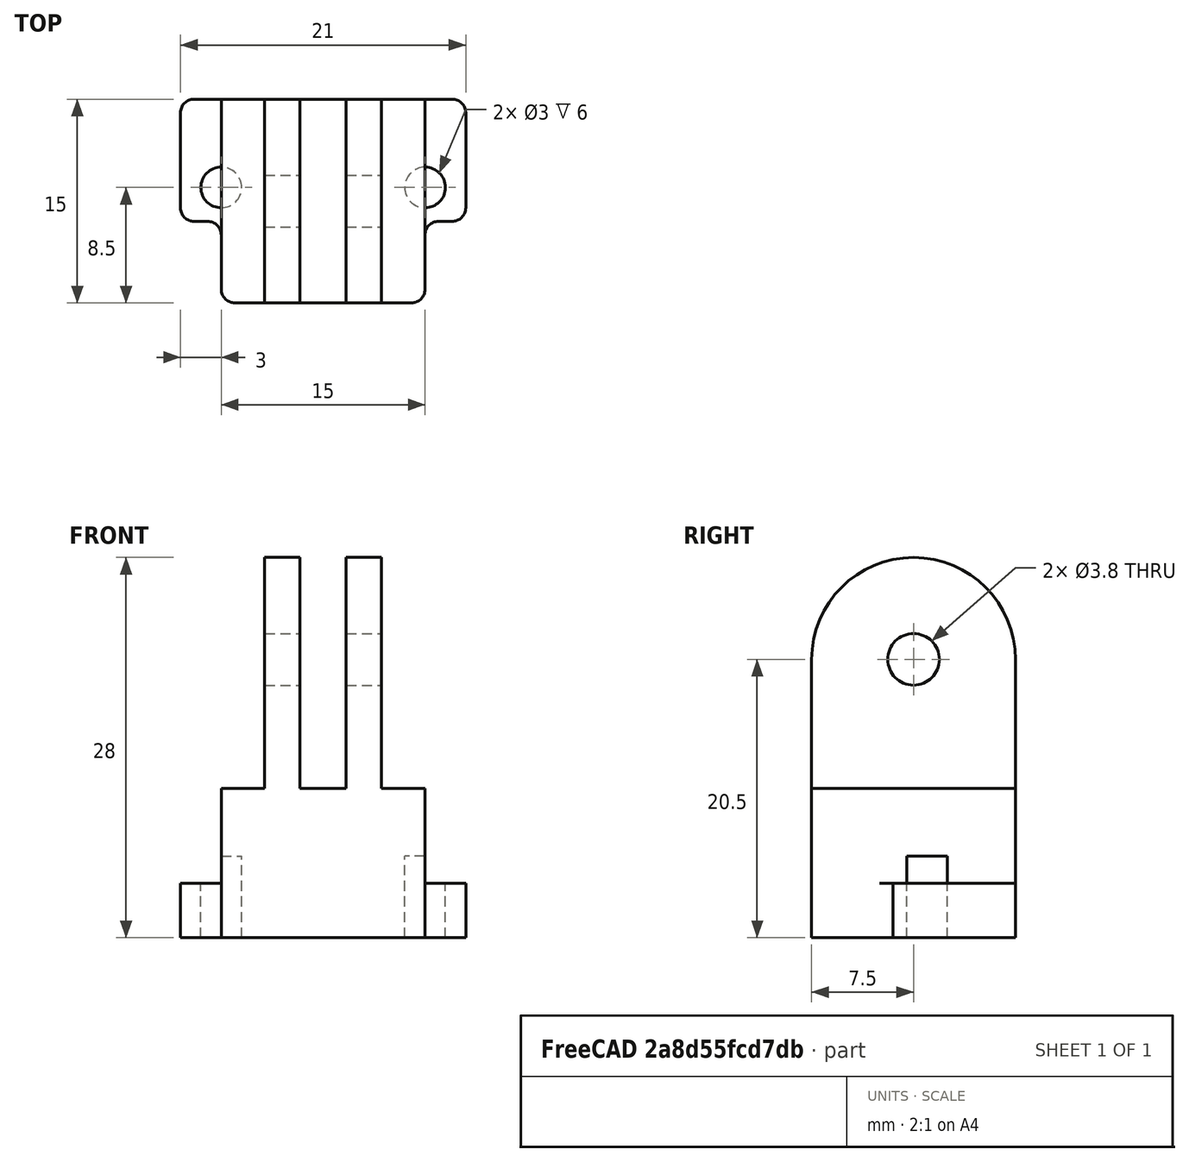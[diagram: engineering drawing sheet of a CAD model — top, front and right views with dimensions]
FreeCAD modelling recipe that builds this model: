
FCSTD DOCUMENT  (FreeCAD 0.19R23578 (Git))
Label: gy-521
License: FreeArt
LicenseURL: http://artlibre.org/licence/lal
objects: Part::Box×2, Spreadsheet::Sheet×1, Part::Cylinder×1, Part::FeaturePython×1, Part::Feature×1, Part::MultiFuse×1, Part::Cut×1, Part::Fillet×1, App::Part×1
note: 8 computed .brp shape members not serialized (recipe doc carries the construction recipe); baked Part::Feature solids carry a one-line shape summary decoded from their .brp

FEATURE [Spreadsheet::Sheet] Spreadsheet  label="p"
  cells = A1=pcb_x; B1(pcb_x)==21mm; A2=pcb_y; B2(pcb_y)==9mm; A3=pcb_z; B3(pcb_z)==1.6mm; A4=hole_dist_x; B4(hole_dist_x)==15mm; A5=hole_offset_y; B5(hole_offset_y)==2.5mm; A6=hole_r; B6(hole_r)==1.5mm; A7=stick_width; B7(stick_width)==15mm; A8=stick_length; B8(stick_length)==10mm; A9=pcb_wall; B9(pcb_wall)==4mm
FEATURE [Part::Cylinder] Cylinder  label="bolt hole"
  Angle = 360
  AttacherType = Attacher::AttachEngine3D
  Height = 10
  Radius = 1.5
  expr: Radius = <<p>>.hole_r
FEATURE [Part::FeaturePython] Array  label="bolt hole array"  # Draft array (typed FeaturePython)
  Angle = 360
  ArrayType = 0
  Axis = (0,0,1)
  Base = -> Cylinder
  Center = (0,0,0)
  Fuse = false
  IntervalAxis = (0,0,0)
  IntervalX = (15,0,0)
  IntervalY = (0,1,0)
  IntervalZ = (0,0,1)
  NumberPolar = 1
  NumberX = 2
  NumberY = 1
  NumberZ = 1
  Placement = pos=(0,8.5,-2) rot=(0,0,1;0rad)
  expr: .Placement.Base.y = <<p>>.stick_width - <<p>>.pcb_y + <<p>>.hole_offset_y
  expr: .IntervalX.x = <<p>>.hole_dist_x
  expr: .Placement.Base.x = (<<p>>.stick_width - <<p>>.hole_dist_x) / 2
FEATURE [Part::Box] Box002  label="stick cube"
  AttacherType = Attacher::AttachEngine3D
  Height = 10
  Length = 15
  Placement = pos=(0,0,2) rot=(0,0,1;0rad)
  Width = 15
  expr: Height = <<p>>.stick_length
  expr: .Placement.Base.z = <<p>>.pcb_back
  expr: Width = <<p>>.stick_width
  expr: Length = <<p>>.stick_width
FEATURE [Part::Feature] Cut001001  label="side 2 cut001"
  Placement = pos=(7.5,7.5,10) rot=(0,0,1;1.5708rad)
  shape: bbox 15 x 15 x 20 mm, 16 faces (baked)
  expr: .Placement.Base.z = <<p>>.stick_length
  expr: .Placement.Base.x = <<p>>.stick_width / 2
  expr: .Placement.Base.y = <<p>>.stick_width / 2
FEATURE [Part::Box] Box003  label="pcb wall"
  AttacherType = Attacher::AttachEngine3D
  Height = 4
  Length = 21
  Placement = pos=(-3,6,2) rot=(0,0,1;0rad)
  Width = 9
  expr: .Placement.Base.y = <<p>>.stick_width - <<p>>.pcb_y
  expr: Height = <<p>>.pcb_wall
  expr: Width = <<p>>.pcb_y
  expr: Length = <<p>>.pcb_x
  expr: .Placement.Base.x = -(<<p>>.pcb_x - <<p>>.stick_width) / 2
  expr: .Placement.Base.z = <<p>>.pcb_wall / 2
FEATURE [Part::MultiFuse] Fusion  label="holder fusion"
  Shapes = -> [Box002,Cut001001,Box003]
FEATURE [Part::Cut] Cut  label="sensor cut"
  Base = -> Fusion
  Tool = -> Array
FEATURE [Part::Fillet] Fillet  label="sensor fillet"
  Base = -> Cut
  Edges = 8 edges r=1: [Edge1,Edge9,Edge11,Edge31,Edge40,Edge52,Edge70,Edge93]
FEATURE [App::Part] Part  label="gy-521 sensor part"
  Group = -> [Fillet]
  Origin = -> Origin
